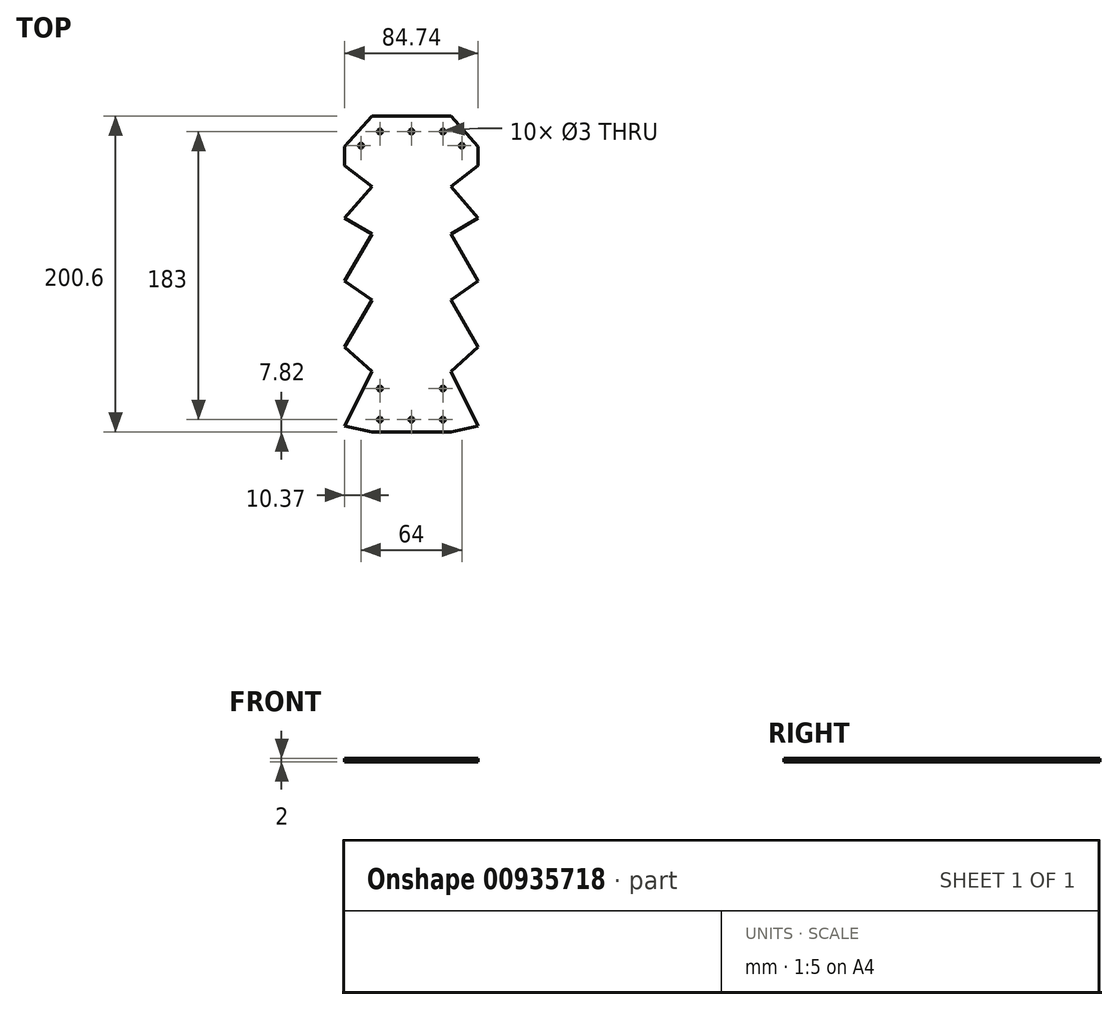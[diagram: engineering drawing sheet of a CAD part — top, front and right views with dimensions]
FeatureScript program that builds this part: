
annotation { "Feature Type Name" : "Feature", "Feature Type Description" : "" }
export const myFeature = defineFeature(function(context is Context, id is Id, definition is map)
    precondition{}
    {
        {
            var Q0;
            Q0=qCreatedBy(makeId("Top.planeOp"),FACE);
            var sketch = newSketch(context, id + "F0", { "sketchPlane" : qUnion([Q0])});
            skCircle(sketch, "E0", {"center": v(-20, -88) * mm, "radius": 1.5 * mm});
            skCircle(sketch, "E1", {"center": v(20, -88) * mm, "radius": 1.5 * mm});
            skCircle(sketch, "E2", {"center": v(0, -88) * mm, "radius": 1.5 * mm});
            skCircle(sketch, "E3", {"center": v(-20, -68.25) * mm, "radius": 1.5 * mm});
            skCircle(sketch, "E4", {"center": v(20, -68.25) * mm, "radius": 1.5 * mm});
            skCircle(sketch, "E5", {"center": v(-20, 95) * mm, "radius": 1.5 * mm});
            skCircle(sketch, "E6", {"center": v(0, 95) * mm, "radius": 1.5 * mm});
            skCircle(sketch, "E7", {"center": v(20, 95) * mm, "radius": 1.5 * mm});
            skCircle(sketch, "E8", {"center": v(-32, 86) * mm, "radius": 1.5 * mm});
            skCircle(sketch, "E9", {"center": v(32, 86) * mm, "radius": 1.5 * mm});
            skLineSegment(sketch, "E10", {"start": v(-25, -95.82) * mm, "end": v(-42.37, -92) * mm});
            skLineSegment(sketch, "E11", {"start": v(-42.37, -92) * mm, "end": v(-25, -57.45) * mm});
            skLineSegment(sketch, "E12", {"start": v(-25, -57.45) * mm, "end": v(-42.37, -42) * mm});
            skLineSegment(sketch, "E13", {"start": v(-42.37, -42) * mm, "end": v(-25, -12.16) * mm});
            skLineSegment(sketch, "E14", {"start": v(-25, -12.16) * mm, "end": v(-42.37, 0) * mm});
            skLineSegment(sketch, "E15", {"start": v(-42.37, 0) * mm, "end": v(-25, 29.92) * mm});
            skLineSegment(sketch, "E16", {"start": v(-25, 29.92) * mm, "end": v(-42.37, 40) * mm});
            skLineSegment(sketch, "E17", {"start": v(-42.37, 40) * mm, "end": v(-25, 60.16) * mm});
            skLineSegment(sketch, "E18", {"start": v(-25, 60.16) * mm, "end": v(-42.37, 73.37) * mm});
            skLineSegment(sketch, "E19", {"start": v(-42.37, 73.37) * mm, "end": v(-42.37, 85.37) * mm});
            skLineSegment(sketch, "E20", {"start": v(-42.37, 85.37) * mm, "end": v(-25, 104.78) * mm});
            skLineSegment(sketch, "E21.MirrorCS", {"start": v(42.37, 85.37) * mm, "end": v(25, 104.78) * mm});
            skLineSegment(sketch, "E22.MirrorCS", {"start": v(42.37, 73.37) * mm, "end": v(42.37, 85.37) * mm});
            skLineSegment(sketch, "E23.MirrorCS", {"start": v(25, 60.16) * mm, "end": v(42.37, 73.37) * mm});
            skLineSegment(sketch, "E24.MirrorCS", {"start": v(42.37, 40) * mm, "end": v(25, 60.16) * mm});
            skLineSegment(sketch, "E25.MirrorCS", {"start": v(25, 29.92) * mm, "end": v(42.37, 40) * mm});
            skLineSegment(sketch, "E26.MirrorCS", {"start": v(42.37, 0) * mm, "end": v(25, 29.92) * mm});
            skLineSegment(sketch, "E27.MirrorCS", {"start": v(25, -12.16) * mm, "end": v(42.37, 0) * mm});
            skLineSegment(sketch, "E28.MirrorCS", {"start": v(42.37, -42) * mm, "end": v(25, -12.16) * mm});
            skLineSegment(sketch, "E29.MirrorCS", {"start": v(25, -57.45) * mm, "end": v(42.37, -42) * mm});
            skLineSegment(sketch, "E30.MirrorCS", {"start": v(42.37, -92) * mm, "end": v(25, -57.45) * mm});
            skLineSegment(sketch, "E31.MirrorCS", {"start": v(25, -95.82) * mm, "end": v(42.37, -92) * mm});
            skLineSegment(sketch, "E32", {"start": v(-25, -95.82) * mm, "end": v(25, -95.82) * mm});
            skLineSegment(sketch, "E33", {"start": v(-25, 104.78) * mm, "end": v(25, 104.78) * mm});
            skSolve(sketch);
        }
        {
            var Q0;
            Q0=makeQuery(id+"F0.imprint","IMPRINT",FACE,{"disambiguationData":[TD([[makeQuery(id+"F0.imprint","IMPRINT",EDGE,{"derivedFrom":sQuery(id+"F0.wireOp",EDGE,"E0")}),-1.0]])]});
            extrude(context, id + "F1", {"entities" : qUnion([Q0]), "depth" : 2 * mm, "offsetDistance" : 25 * mm});
        }
    });
